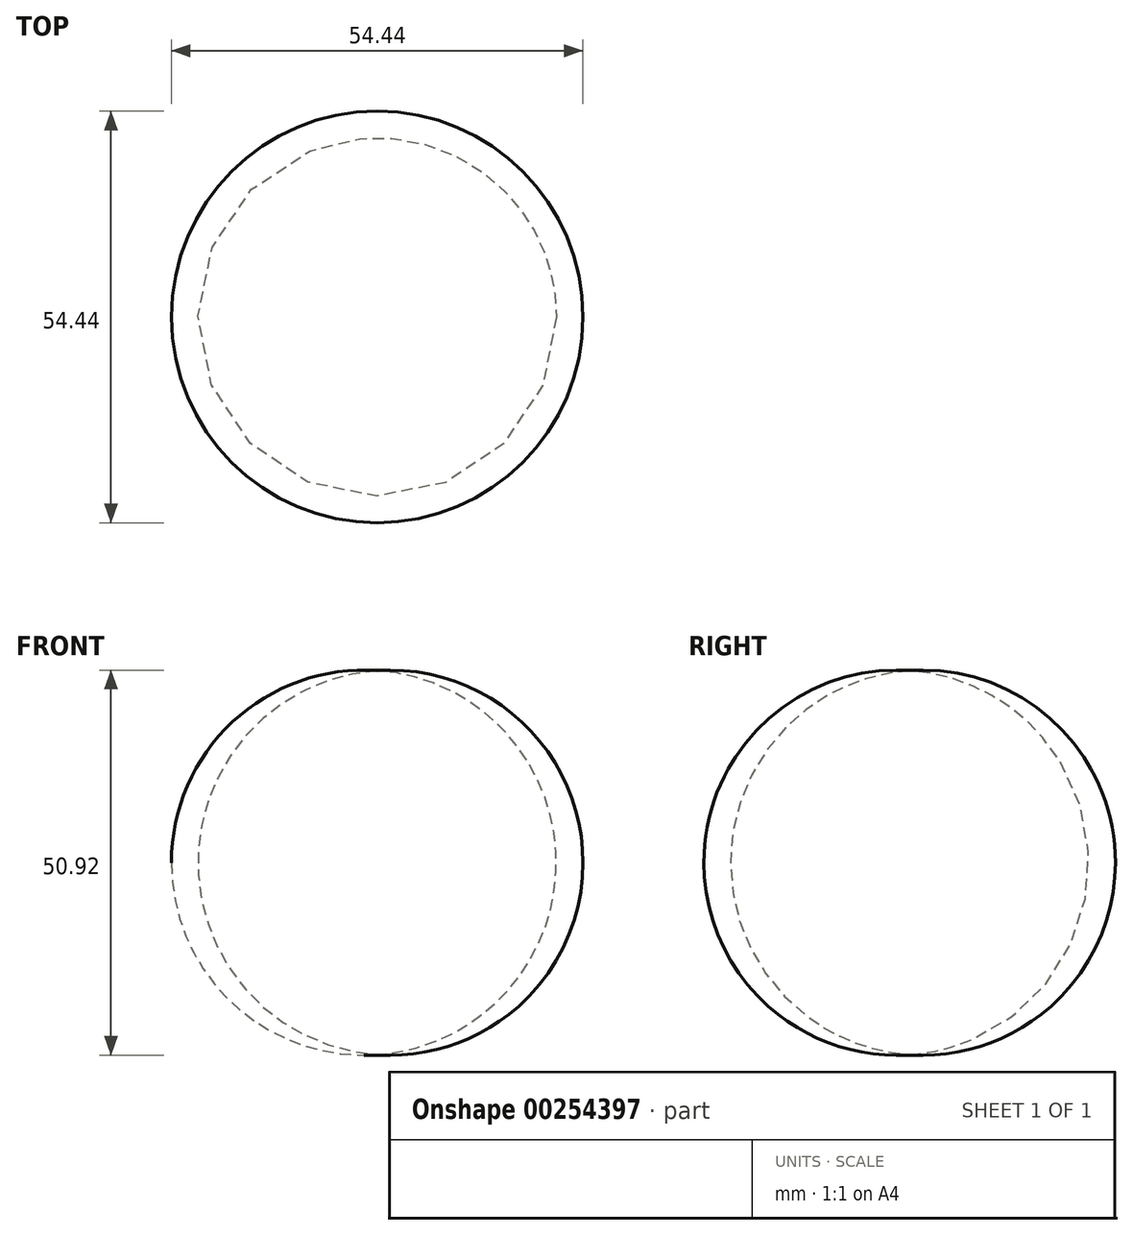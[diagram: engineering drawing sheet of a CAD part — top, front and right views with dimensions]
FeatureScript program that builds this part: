
annotation { "Feature Type Name" : "Feature", "Feature Type Description" : "" }
export const myFeature = defineFeature(function(context is Context, id is Id, definition is map)
    precondition{}
    {
        {
            var Q0;
            Q0=qCreatedBy(makeId("Front.planeOp"),FACE);
            var sketch = newSketch(context, id + "F0", { "sketchPlane" : qUnion([Q0])});
            skLineSegment(sketch, "E0", {"start": v(0, 0) * mm, "end": v(0, 50.8) * mm});
            skArc(sketch, "E1", {"start": v(0, 50.8) * mm, "mid": v(-27.22, 25.4) * mm, "end": v(0, 0) * mm});
            skSolve(sketch);
        }
        {
            var Q0;
            Q0=makeQuery(id+"F0.imprint","IMPRINT",FACE,{"disambiguationData":[TD([[makeQuery(id+"F0.imprint","IMPRINT",EDGE,{"derivedFrom":sQuery(id+"F0.wireOp",EDGE,"E0")}),1.0]])]});
            var Q1;
            Q1=sQuery(id+"F0.wireOp",EDGE,"E0");
            revolve(context, id + "F1", {"entities" : qUnion([Q0]), "axis" : qUnion([Q1]), "revolveType" : RevolveType.FULL});
        }
    });
